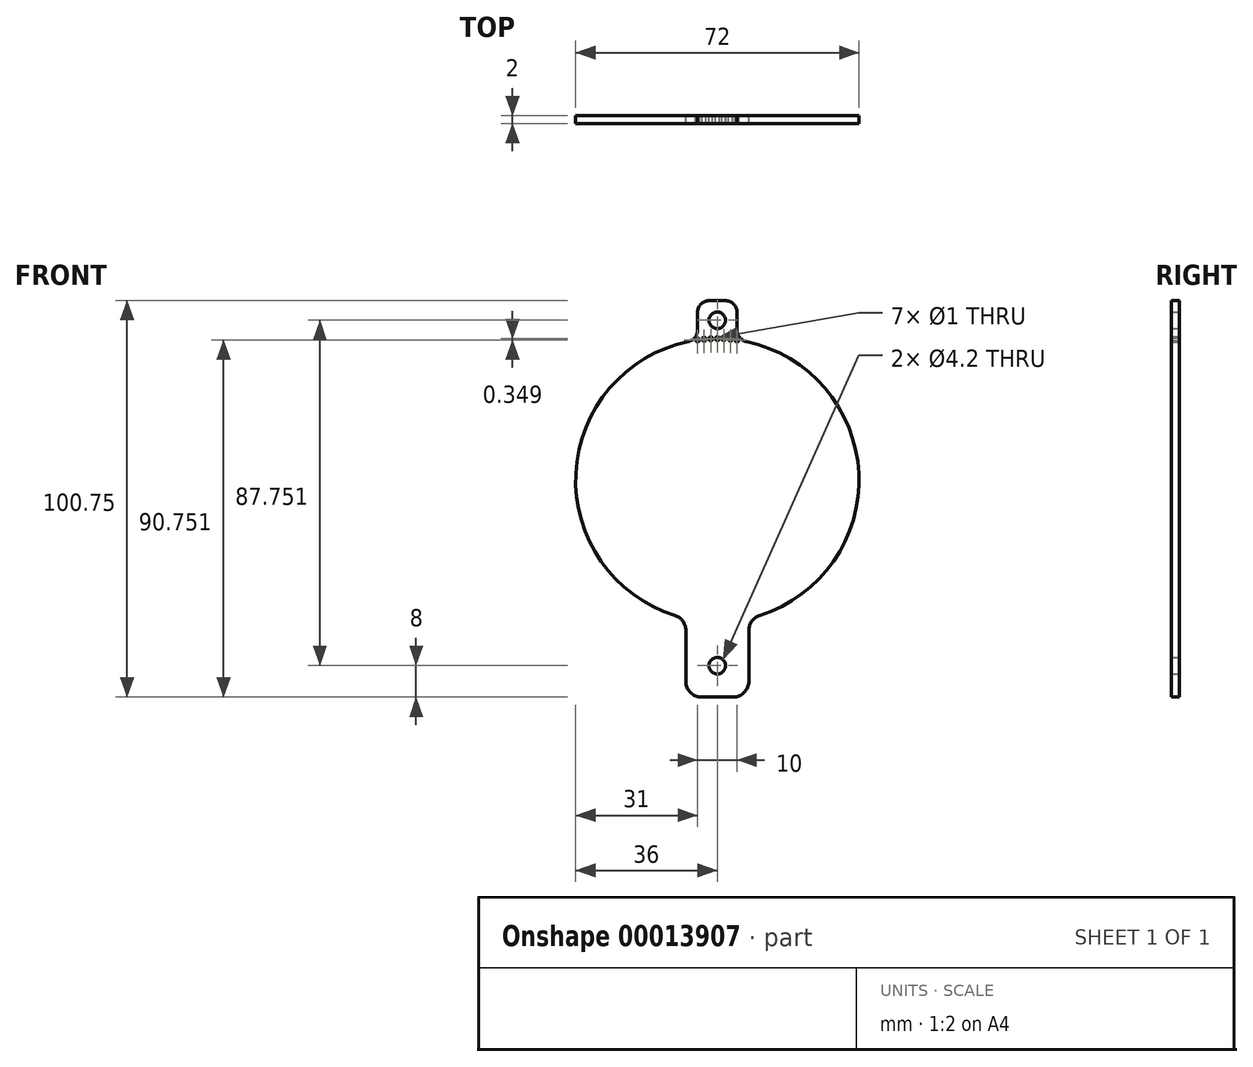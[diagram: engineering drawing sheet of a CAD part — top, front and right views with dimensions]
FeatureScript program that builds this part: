
annotation { "Feature Type Name" : "Feature", "Feature Type Description" : "" }
export const myFeature = defineFeature(function(context is Context, id is Id, definition is map)
    precondition{}
    {
        {
            var Q0;
            Q0=qCreatedBy(makeId("Front.planeOp"),FACE);
            var sketch = newSketch(context, id + "F0", { "sketchPlane" : qUnion([Q0])});
            skLineSegment(sketch, "E0.top", {"start": v(-4, -8) * mm, "end": v(4, -8) * mm});
            skLineSegment(sketch, "E0.left", {"start": v(-8, 8.94) * mm, "end": v(-8, -4) * mm});
            skLineSegment(sketch, "E0.right", {"start": v(8, 8.94) * mm, "end": v(8, -4) * mm});
            skLineSegment(sketch, "E1", {"start": v(0, 12) * mm, "end": v(0, -8) * mm, "construction": true});
            skPoint(sketch, "E1.startSnap0", {"position": v(0, 12) * mm});
            skLineSegment(sketch, "E2", {"start": v(8, 0) * mm, "end": v(-8, 0) * mm, "construction": true});
            skArc(sketch, "E3", {"start": v(10.8, 12.76) * mm, "mid": v(35.96, 48.86) * mm, "end": v(7.38, 82.33) * mm});
            skCircle(sketch, "E4", {"center": v(0, 0) * mm, "radius": 2.1 * mm});
            skPoint(sketch, "E5.visualSharp", {"position": v(-8, -8) * mm});
            skArc(sketch, "E5.filletArc", {"start": v(-8, -4) * mm, "mid": v(-6.83, -6.83) * mm, "end": v(-4, -8) * mm});
            skPoint(sketch, "E6.visualSharp", {"position": v(8, -8) * mm});
            skArc(sketch, "E6.filletArc", {"start": v(4, -8) * mm, "mid": v(6.83, -6.83) * mm, "end": v(8, -4) * mm});
            skPoint(sketch, "E7.visualSharp", {"position": v(8, 12) * mm});
            skArc(sketch, "E7.filletArc", {"start": v(10.8, 12.76) * mm, "mid": v(8.78, 11.3) * mm, "end": v(8, 8.94) * mm});
            skPoint(sketch, "E8.visualSharp", {"position": v(-8, 12) * mm});
            skArc(sketch, "E8.filletArc", {"start": v(-8, 8.94) * mm, "mid": v(-8.78, 11.3) * mm, "end": v(-10.8, 12.76) * mm});
            skLineSegment(sketch, "E9.top", {"start": v(-2, 92.75) * mm, "end": v(2, 92.75) * mm});
            skLineSegment(sketch, "E9.left", {"start": v(-5, 85.27) * mm, "end": v(-5, 89.75) * mm});
            skLineSegment(sketch, "E9.right", {"start": v(5, 85.27) * mm, "end": v(5, 89.75) * mm});
            skArc(sketch, "E10.trimOffspring", {"start": v(-7.38, 82.33) * mm, "mid": v(-35.96, 48.86) * mm, "end": v(-10.8, 12.76) * mm});
            skPoint(sketch, "E11.visualSharp", {"position": v(-5, 82.75) * mm});
            skArc(sketch, "E11.filletArc", {"start": v(-7.38, 82.33) * mm, "mid": v(-5.67, 83.38) * mm, "end": v(-5, 85.27) * mm});
            skPoint(sketch, "E12.visualSharp", {"position": v(-5, 92.75) * mm});
            skArc(sketch, "E12.filletArc", {"start": v(-2, 92.75) * mm, "mid": v(-4.12, 91.87) * mm, "end": v(-5, 89.75) * mm});
            skPoint(sketch, "E13.visualSharp", {"position": v(5, 92.75) * mm});
            skArc(sketch, "E13.filletArc", {"start": v(5, 89.75) * mm, "mid": v(4.12, 91.87) * mm, "end": v(2, 92.75) * mm});
            skPoint(sketch, "E14.visualSharp", {"position": v(5, 82.75) * mm});
            skArc(sketch, "E14.filletArc", {"start": v(5, 85.27) * mm, "mid": v(5.67, 83.38) * mm, "end": v(7.38, 82.33) * mm});
            skCircle(sketch, "E15", {"center": v(0, 87.75) * mm, "radius": 2.1 * mm});
            skCircle(sketch, "E16", {"center": v(-5, 82.75) * mm, "radius": 0.5 * mm});
            skCircle(sketch, "E17", {"center": v(-3.34, 82.94) * mm, "radius": 0.5 * mm});
            skCircle(sketch, "E18", {"center": v(-1.67, 83.06) * mm, "radius": 0.5 * mm});
            skCircle(sketch, "E19", {"center": v(0, 83.1) * mm, "radius": 0.5 * mm});
            skCircle(sketch, "E20", {"center": v(0, 47.1) * mm, "radius": 36 * mm, "construction": true});
            skCircle(sketch, "E21", {"center": v(1.67, 83.06) * mm, "radius": 0.5 * mm});
            skCircle(sketch, "E22", {"center": v(3.34, 82.94) * mm, "radius": 0.5 * mm});
            skCircle(sketch, "E23", {"center": v(5, 82.75) * mm, "radius": 0.5 * mm});
            skLineSegment(sketch, "E24", {"start": v(-5, 82.75) * mm, "end": v(-3.34, 82.94) * mm, "construction": true});
            skLineSegment(sketch, "E25", {"start": v(-3.34, 82.94) * mm, "end": v(-1.67, 83.06) * mm, "construction": true});
            skLineSegment(sketch, "E26", {"start": v(-1.67, 83.06) * mm, "end": v(0, 83.1) * mm, "construction": true});
            skSolve(sketch);
        }
        {
            var Q0;
            Q0 = qSketchRegion(id + "F0", true);
            extrude(context, id + "F1", {"entities" : qUnion([Q0]), "depth" : 2 * mm});
        }
    });
